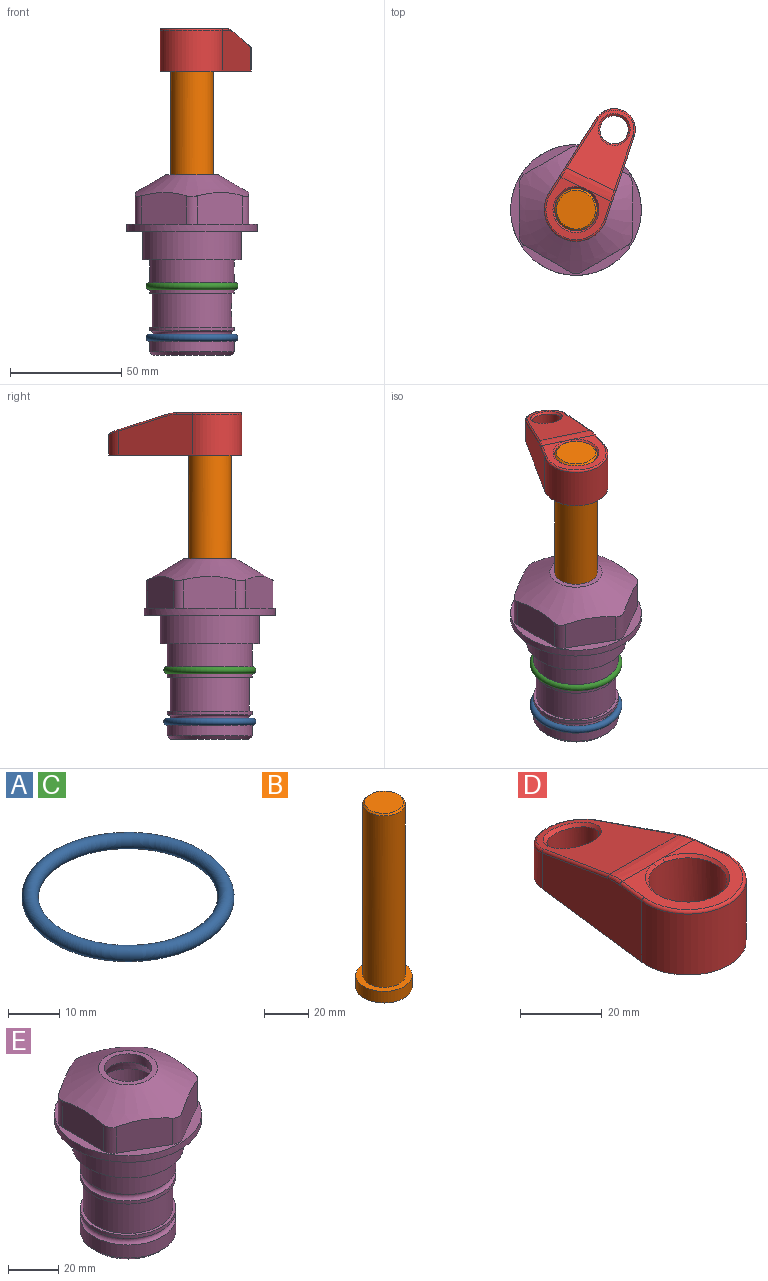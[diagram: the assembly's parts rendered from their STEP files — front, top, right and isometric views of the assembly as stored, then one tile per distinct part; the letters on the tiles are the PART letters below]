
ASSEMBLY  parts=5 mates=4
PART A: 1 faces, bbox 44.7x44.7x3.2 mm
  f0: torus R=19.05mm, axis (0,0,1), area 1193.9mm2
PART B: 6 faces, bbox 25.4x25.4x101.6 mm
  f0: plane 17.46x17.46mm, normal (0,0,1), area 239.5mm2, adj f5
  f1: plane 25.4x25.4mm, normal (0,0,-1), area 506.7mm2, adj f2
  f2: cylinder r=12.7mm len=25.4mm, axis (0,0,1), area 506.7mm2, adj f1,f3
  f3: plane 25.4x25.4mm, normal (0,0,1), area 221.7mm2, adj f2,f4
  f4: cylinder r=9.53mm len=94.46mm, axis (0,0,1), area 5653mm2, adj f3,f5
  f5: cone r=8.73mm half-angle=45deg, axis (0,0,-1), area 64.4mm2, adj f0,f4
PART C: same geometry as A
PART D: 31 faces, bbox 31.7x65.5x19.8 mm
  f0: plane 39.12x18.26mm, normal (0.99,0.12,0), area 612.2mm2, adj f1,f4,f7,f11,f13,f15
  f1: cylinder r=9.53mm len=18.91mm, axis (0,0,-1), area 296.1mm2, adj f0,f2,f7,f17
  f2: plane 39.12x18.26mm, normal (-0.99,0.12,0), area 612.2mm2, adj f1,f4,f7,f12,f14,f16
  f3: cylinder r=6.35mm len=12.7mm, axis (0,0,-1), area 362.4mm2, adj f7,f18
  f4: cylinder r=14.29mm len=28.58mm, axis (0,0,-1), area 882.2mm2, adj f0,f2,f7,f10
  f5: cylinder r=9.53mm len=19.05mm, axis (0,0,-1), area 1092.6mm2, adj f7,f19,f20
  f6: plane 26.99x23.69mm, normal (0,0,1), area 216.2mm2, adj f9,f10,f11,f12,f19
  f7: plane 63.5x28.58mm, normal (0,0,-1), area 661.8mm2, adj f0,f1,f2,f3,f4,f5,f22,f23
  f8: plane 33.52x23.6mm, normal (0,0.26,0.97), area 486mm2, adj f9,f15,f16,f17,f18
  f9: cylinder r=19.05mm len=24.72mm, axis (1,0,0), area 120.4mm2, adj f6,f8,f13,f14,f20
  f10: torus R=13.49mm, axis (0,0,1), area 59mm2, adj f4,f6,f11,f12
  f11: cylinder r=0.79mm len=8.67mm, axis (0.12,-0.99,0), area 10.8mm2, adj f0,f6,f10,f13
  f12: cylinder r=0.79mm len=8.67mm, axis (0.12,0.99,0), area 10.8mm2, adj f2,f6,f10,f14
  f13: bspline ~4.95x1.42mm, area 6.1mm2, adj f0,f9,f11,f15
  f14: bspline ~4.95x1.42mm, area 6.1mm2, adj f2,f9,f12,f16
  f15: cylinder r=0.79mm len=25.95mm, axis (0.12,-0.96,0.26), area 32.9mm2, adj f0,f8,f13,f17
  f16: cylinder r=0.79mm len=25.95mm, axis (0.12,0.96,-0.26), area 32.9mm2, adj f2,f8,f14,f17
  f17: bspline ~18.91x8.38mm, area 30mm2, adj f1,f8,f15,f16
  f18: bspline ~14.29x14.29mm, area 48.3mm2, adj f3,f8
  f19: cone r=9.53mm half-angle=45deg, axis (0,0,1), area 66.5mm2, adj f5,f6,f20
  f20: bspline ~3.22x0.96mm, area 3.5mm2, adj f5,f9,f19
  f21: plane 2.75x2.72mm, normal (0,0,-1), area 2.9mm2, adj f23,f25,f28
  f22: plane 23.05x15.88mm, normal (-0.99,-0.12,0), area 323.6mm2, adj f7,f25,f26,f27,f28,f29
  f23: plane 23.05x15.88mm, normal (0.99,-0.12,0), area 323.6mm2, adj f7,f21,f25,f27,f28,f30
  f24: cylinder r=9.53mm len=10.69mm, axis (0,0,-1), area 114.7mm2, adj f7,f27,f29,f30
  f25: cylinder r=12.7mm len=20.59mm, axis (0,0,-1), area 381.1mm2, adj f7,f21,f22,f23,f26,f28
  f26: plane 2.75x2.72mm, normal (0,0,-1), area 2.9mm2, adj f22,f25,f28
  f27: plane 19.72x18.37mm, normal (0,-0.26,-0.97), area 291.8mm2, adj f22,f23,f24,f28,f29,f30
  f28: cylinder r=15.88mm len=19.92mm, axis (1,0,0), area 54.8mm2, adj f21,f22,f23,f25,f26,f27
  f29: cylinder r=1.59mm len=11mm, axis (0,0,-1), area 34.7mm2, adj f7,f22,f24,f27
  f30: cylinder r=1.59mm len=11mm, axis (0,0,-1), area 34.7mm2, adj f7,f23,f24,f27
PART E: 36 faces, bbox 58.7x58.7x81 mm
  f0: cylinder r=17.78mm len=35.56mm, axis (0,0,1), area 1670.8mm2, adj f23,f24,f31
  f1: cylinder r=19.05mm len=38.1mm, axis (0,0,1), area 1191.9mm2, adj f26,f27,f30
  f2: plane 58.66x58.66mm, normal (0,0,-1), area 1150.6mm2, adj f3,f28
  f3: cylinder r=29.33mm len=58.66mm, axis (0,0,-1), area 585.1mm2, adj f2,f4
  f4: plane 58.66x58.66mm, normal (0,0,1), area 475.9mm2, adj f3,f5,f6,f7,f8,f9,f10,f11
  f5: plane 20.32x14.34mm, normal (-0.5,0.87,0), area 324.4mm2, adj f4,f15,f16,f17
  f6: plane 20.32x14.34mm, normal (0.5,0.87,0), area 324.4mm2, adj f4,f14,f15,f17
  f7: plane 23.48x14.34mm, normal (1,0,0), area 324.4mm2, adj f4,f13,f14,f17
  f8: plane 20.32x14.34mm, normal (0.5,-0.87,0), area 324.4mm2, adj f4,f12,f13,f17
  f9: plane 20.32x14.34mm, normal (-0.5,-0.87,0), area 324.4mm2, adj f4,f11,f12,f17
  f10: plane 23.48x14.34mm, normal (-1,0,0), area 324.4mm2, adj f4,f11,f16,f17
  f11: cylinder r=5.08mm len=12.85mm, axis (0,0,-1), area 67.2mm2, adj f4,f9,f10,f17
  f12: cylinder r=5.08mm len=12.85mm, axis (0,0,-1), area 67.2mm2, adj f4,f8,f9,f17
  f13: cylinder r=5.08mm len=12.85mm, axis (0,0,-1), area 67.2mm2, adj f4,f7,f8,f17
  f14: cylinder r=5.08mm len=12.85mm, axis (0,0,-1), area 67.2mm2, adj f4,f6,f7,f17
  f15: cylinder r=5.08mm len=12.85mm, axis (0,0,-1), area 67.2mm2, adj f4,f5,f6,f17
  f16: cylinder r=5.08mm len=12.85mm, axis (0,0,-1), area 67.2mm2, adj f4,f5,f10,f17
  f17: cone r=11.73mm half-angle=60deg, axis (0,0,-1), area 2071.8mm2, adj f5,f6,f7,f8,f9,f10,f11,f12
  f18: plane 23.46x23.46mm, normal (0,0,1), area 147.4mm2, adj f17,f35
  f19: plane 34.93x34.93mm, normal (0,0,-1), area 958mm2, adj f29
  f20: cylinder r=19.05mm len=38.1mm, axis (0,0,1), area 760.1mm2, adj f21,f29
  f21: torus R=19.05mm, axis (0,0,1), area 565.3mm2, adj f20,f22
  f22: cylinder r=19.05mm len=38.1mm, axis (0,0,1), area 190mm2, adj f21,f23
  f23: plane 38.1x38.1mm, normal (0,0,1), area 146.9mm2, adj f0,f22
  f24: plane 38.1x38.1mm, normal (0,0,-1), area 146.9mm2, adj f0,f25
  f25: cylinder r=19.05mm len=38.1mm, axis (0,0,1), area 190mm2, adj f24,f26
  f26: torus R=19.05mm, axis (0,0,1), area 565.3mm2, adj f1,f25
  f27: plane 44.45x44.45mm, normal (0,0,-1), area 411.7mm2, adj f1,f28
  f28: cylinder r=22.23mm len=44.45mm, axis (0,0,1), area 1773.5mm2, adj f2,f27
  f29: cone r=19.05mm half-angle=45deg, axis (0,0,1), area 257.5mm2, adj f19,f20
  f30: cylinder r=3.17mm len=6.75mm, axis (-1,0,0), area 128mm2, adj f1,f33
  f31: cylinder r=3.17mm len=6.35mm, axis (-1,0,0), area 102.5mm2, adj f0,f33
  f32: plane 25.4x25.4mm, normal (0,0,1), area 506.7mm2, adj f33
  f33: cylinder r=12.7mm len=66.42mm, axis (0,0,-1), area 5236.2mm2, adj f30,f31,f32,f34
  f34: cone r=9.53mm half-angle=30deg, axis (0,0,-1), area 443.4mm2, adj f33,f35
  f35: cylinder r=9.53mm len=19.05mm, axis (0,0,-1), area 240.9mm2, adj f18,f34
PLACE A t=(0,0,-23.18)mm
PLACE B rot(axis=(0,0,-1),25.5deg) t=(0,0,27.55)mm
PLACE C at identity
PLACE D rot(axis=(0,0,-1),25.5deg) t=(0,0,27.55)mm
PLACE E at identity fixed
MATE fastened A.f0 <-> E.f0  axis (0,0,1) through (0,0,-47.69)mm
MATE fastened B.f2 <-> D.f4  axis (0,0,1) through (0,0,91.05)mm
MATE fastened C.f0 <-> E.f0  axis (0,0,1) through (0,0,-24.51)mm
MATE cylindrical E.f0 <-> B.f2  axis (0,0,1) through (0,0,-50.55)mm
